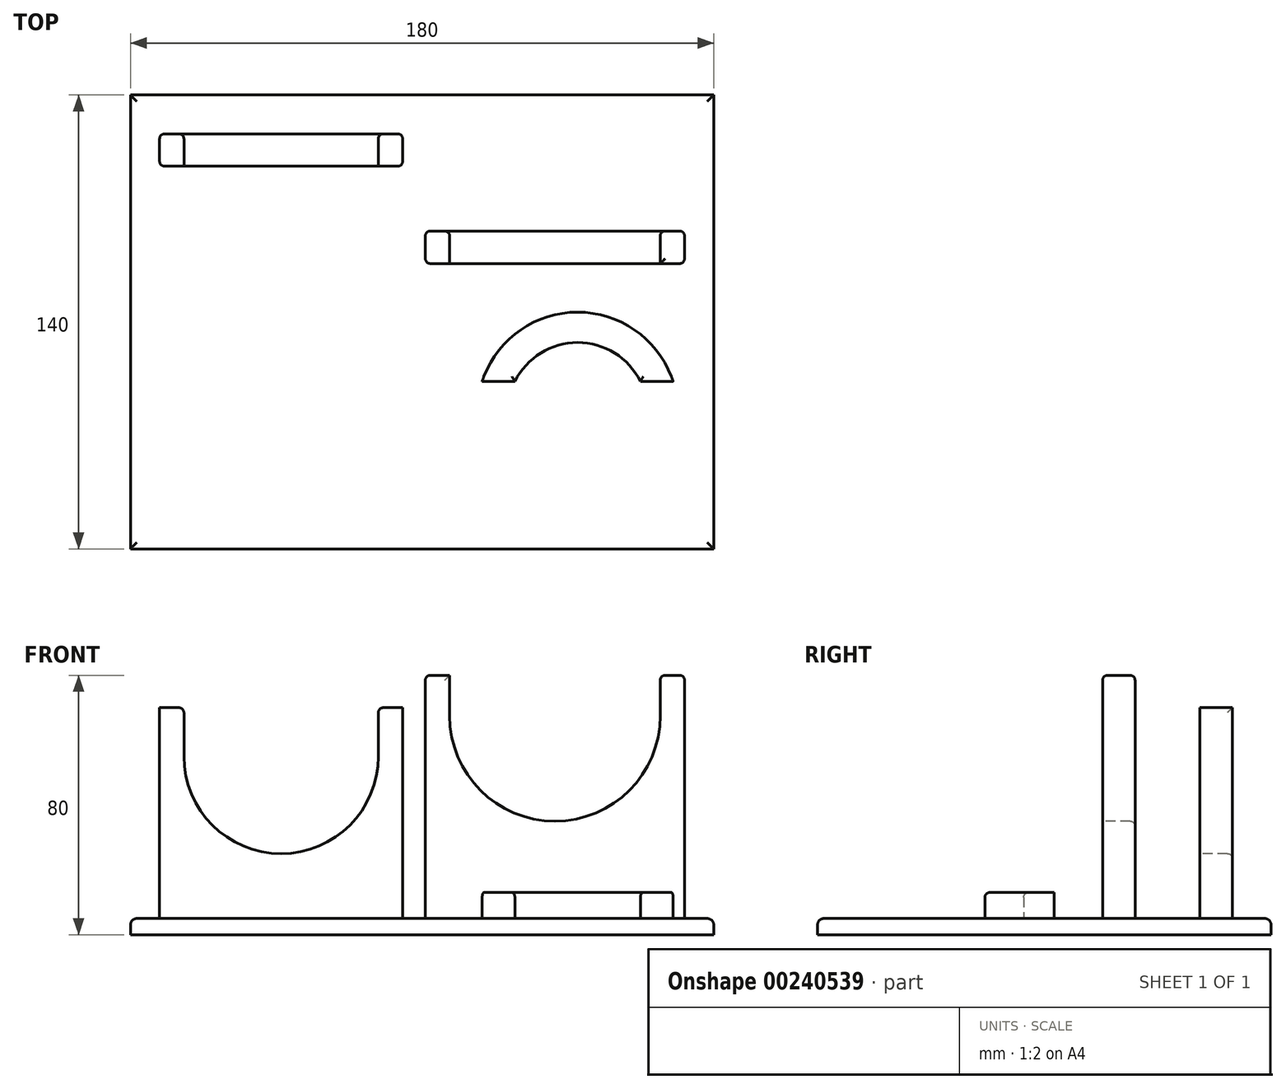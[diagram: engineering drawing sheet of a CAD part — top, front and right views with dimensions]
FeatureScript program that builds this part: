
annotation { "Feature Type Name" : "Feature", "Feature Type Description" : "" }
export const myFeature = defineFeature(function(context is Context, id is Id, definition is map)
    precondition{}
    {
        {
            var Q0;
            Q0=qCreatedBy(makeId("Top.planeOp"),FACE);
            var sketch = newSketch(context, id + "F5", { "sketchPlane" : qUnion([Q0])});
            skLineSegment(sketch, "E0.bottom", {"start": v(-84.6, 104.11) * mm, "end": v(95.4, 104.11) * mm});
            skLineSegment(sketch, "E0.top", {"start": v(-84.6, -35.89) * mm, "end": v(95.4, -35.89) * mm});
            skLineSegment(sketch, "E0.left", {"start": v(-84.6, 104.11) * mm, "end": v(-84.6, -35.89) * mm});
            skLineSegment(sketch, "E0.right", {"start": v(95.4, 104.11) * mm, "end": v(95.4, -35.89) * mm});
            skSolve(sketch);
        }
        {
            var Q0;
            Q0 = qSketchRegion(id + "F5", true);
            extrude(context, id + "F0", {"entities" : qUnion([Q0]), "depth" : 5 * mm});
        }
        {
            var Q0;
            Q0=makeQuery(id+"F0.opExtrude","CAP_EDGE",EDGE,{"disambiguationData":[OSD([sQuery(id+"F5.wireOp",EDGE,"E0.top")])],"isStart":false});
            var Q1;
            Q1=makeQuery(id+"F0.opExtrude","CAP_EDGE",EDGE,{"disambiguationData":[OSD([sQuery(id+"F5.wireOp",EDGE,"E0.right")])],"isStart":false});
            var Q2;
            Q2=makeQuery(id+"F0.opExtrude","CAP_EDGE",EDGE,{"disambiguationData":[OSD([sQuery(id+"F5.wireOp",EDGE,"E0.left")])],"isStart":false});
            var Q3;
            Q3=makeQuery(id+"F0.opExtrude","CAP_EDGE",EDGE,{"disambiguationData":[OSD([sQuery(id+"F5.wireOp",EDGE,"E0.bottom")])],"isStart":false});
            fillet(context, id + "F1", {"entities" : qUnion([Q0, Q1, Q2, Q3]), "radius" : 2 * mm, "tangentPropagation" : true, "allowEdgeOverflow" : false});
        }
        {
            var Q0;
            Q0=makeQuery(id+"F0.opExtrude","CAP_FACE",FACE,{"disambiguationData":[OSD([sQuery(id+"F5.wireOp",EDGE,"E0.bottom"),sQuery(id+"F5.wireOp",EDGE,"E0.top"),sQuery(id+"F5.wireOp",EDGE,"E0.left"),sQuery(id+"F5.wireOp",EDGE,"E0.right")])],"isStart":false});
            var sketch = newSketch(context, id + "F6", { "sketchPlane" : qUnion([Q0])});
            skLineSegment(sketch, "E1.bottom", {"start": v(23.95, 15.78) * mm, "end": v(34.04, 15.78) * mm});
            skLineSegment(sketch, "E2.trimOffspring", {"start": v(72.77, 15.78) * mm, "end": v(82.86, 15.78) * mm});
            skArc(sketch, "E3.trimOffspring", {"start": v(72.77, 15.78) * mm, "mid": v(53.4, 27.76) * mm, "end": v(34.04, 15.78) * mm});
            skArc(sketch, "E4.trimOffspring", {"start": v(82.86, 15.78) * mm, "mid": v(53.4, 37.11) * mm, "end": v(23.95, 15.78) * mm});
            skSolve(sketch);
        }
        {
            var Q0;
            Q0 = qSketchRegion(id + "F6", true);
            extrude(context, id + "F7", {"entities" : qUnion([Q0]), "operationType" : NewBodyOperationType.ADD, "depth" : 8 * mm});
        }
        {
            var Q0;
            Q0=makeQuery(id+"F0.opExtrude","CAP_FACE",FACE,{"disambiguationData":[OSD([sQuery(id+"F5.wireOp",EDGE,"E0.bottom"),sQuery(id+"F5.wireOp",EDGE,"E0.top"),sQuery(id+"F5.wireOp",EDGE,"E0.left"),sQuery(id+"F5.wireOp",EDGE,"E0.right")])],"isStart":false});
            var sketch = newSketch(context, id + "F8", { "sketchPlane" : qUnion([Q0])});
            skLineSegment(sketch, "E5.bottom", {"start": v(-75.6, 92.11) * mm, "end": v(-0.6, 92.11) * mm});
            skLineSegment(sketch, "E5.top", {"start": v(-75.6, 82.11) * mm, "end": v(-0.6, 82.11) * mm});
            skLineSegment(sketch, "E5.left", {"start": v(-75.6, 92.11) * mm, "end": v(-75.6, 82.11) * mm});
            skLineSegment(sketch, "E5.right", {"start": v(-0.6, 92.11) * mm, "end": v(-0.6, 82.11) * mm});
            skLineSegment(sketch, "E6.bottom", {"start": v(6.4, 62.11) * mm, "end": v(86.4, 62.11) * mm});
            skLineSegment(sketch, "E6.top", {"start": v(6.4, 52.11) * mm, "end": v(86.4, 52.11) * mm});
            skLineSegment(sketch, "E6.left", {"start": v(6.4, 62.11) * mm, "end": v(6.4, 52.11) * mm});
            skLineSegment(sketch, "E6.right", {"start": v(86.4, 62.11) * mm, "end": v(86.4, 52.11) * mm});
            skArc(sketch, "E7.0", {"start": v(82.86, 15.78) * mm, "mid": v(53.4, 37.11) * mm, "end": v(23.95, 15.78) * mm});
            skSolve(sketch);
        }
        {
            var Q0;
            Q0 = qSketchRegion(id + "F8", true);
            extrude(context, id + "F9", {"entities" : qUnion([Q0]), "operationType" : NewBodyOperationType.ADD, "depth" : 75 * mm});
        }
        {
            var Q0;
            Q0 = qSketchRegion(id + "F8", true);
            extrude(context, id + "F10", {"entities" : qUnion([Q0]), "operationType" : NewBodyOperationType.ADD, "depth" : 75 * mm});
        }
        {
            var Q0;
            Q0=makeQuery(id+"F9.opExtrude","SWEPT_FACE",FACE,{"disambiguationData":[OSD([sQuery(id+"F8.wireOp",EDGE,"E6.top")])]});
            var sketch = newSketch(context, id + "F2", { "sketchPlane" : qUnion([Q0])});
            skArc(sketch, "E8", {"start": v(13.9, 67.5) * mm, "mid": v(46.4, 35) * mm, "end": v(78.9, 67.5) * mm});
            skLineSegment(sketch, "E9.0", {"start": v(13.9, 80) * mm, "end": v(78.9, 80) * mm});
            skPoint(sketch, "E9.1", {"position": v(6.4, 80) * mm});
            skLineSegment(sketch, "E10", {"start": v(13.9, 80) * mm, "end": v(13.9, 67.5) * mm});
            skLineSegment(sketch, "E11", {"start": v(78.9, 67.5) * mm, "end": v(78.9, 80) * mm});
            skPoint(sketch, "E9.2.end.orphan", {"position": v(86.4, 5) * mm});
            skPoint(sketch, "E9.2.start.orphan", {"position": v(86.4, 80) * mm});
            skPoint(sketch, "E9.3.end.orphan", {"position": v(6.4, 5) * mm});
            skSolve(sketch);
        }
        {
            var Q0;
            Q0 = qSketchRegion(id + "F2", true);
            extrude(context, id + "F11", {"entities" : qUnion([Q0]), "operationType" : NewBodyOperationType.REMOVE, "oppositeDirection" : true, "depth" : 25 * mm});
        }
        {
            var Q0;
            Q0=makeQuery(id+"F9.opExtrude","SWEPT_FACE",FACE,{"disambiguationData":[OSD([sQuery(id+"F8.wireOp",EDGE,"E5.top")])]});
            var sketch = newSketch(context, id + "F3", { "sketchPlane" : qUnion([Q0])});
            skArc(sketch, "E12", {"start": v(-68.1, 55) * mm, "mid": v(-38.1, 25) * mm, "end": v(-8.1, 55) * mm});
            skLineSegment(sketch, "E13.0", {"start": v(-0.6, 80) * mm, "end": v(-0.6, 5) * mm});
            skLineSegment(sketch, "E13.1", {"start": v(-75.6, 80) * mm, "end": v(-0.6, 80) * mm});
            skLineSegment(sketch, "E13.2", {"start": v(-75.6, 80) * mm, "end": v(-75.6, 5) * mm});
            skLineSegment(sketch, "E14", {"start": v(-68.1, 55) * mm, "end": v(-68.1, 70) * mm});
            skLineSegment(sketch, "E15", {"start": v(-8.1, 55) * mm, "end": v(-8.1, 70) * mm});
            skLineSegment(sketch, "E16", {"start": v(-0.6, 70) * mm, "end": v(-8.1, 70) * mm});
            skLineSegment(sketch, "E17.trimOffspring", {"start": v(-75.6, 70) * mm, "end": v(-68.1, 70) * mm});
            skLineSegment(sketch, "E18.trimOffspring", {"start": v(-68.1, 70) * mm, "end": v(-75.6, 70) * mm});
            skLineSegment(sketch, "E19.trimOffspring", {"start": v(-8.1, 70) * mm, "end": v(-0.6, 70) * mm});
            skSolve(sketch);
        }
        {
            var Q0;
            Q0 = qSketchRegion(id + "F3", true);
            extrude(context, id + "F4", {"entities" : qUnion([Q0]), "operationType" : NewBodyOperationType.REMOVE, "oppositeDirection" : true, "depth" : 25 * mm});
        }
        {
            var Q0;
            Q0=makeQuery(id+"F9.opExtrude","SWEPT_EDGE",EDGE,{"disambiguationData":[OSD([sQuery(id+"F8.wireOp",EDGE,"E6.top"),sQuery(id+"F8.wireOp",EDGE,"E6.right")])]});
            var Q1;
            Q1=makeQuery(id+"F9.opExtrude","SWEPT_EDGE",EDGE,{"disambiguationData":[OSD([sQuery(id+"F8.wireOp",EDGE,"E6.bottom"),sQuery(id+"F8.wireOp",EDGE,"E6.right")])]});
            var Q2;
            Q2=makeQuery(id+"F11.boolean.opBoolean","COPY",EDGE,{"derivedFrom":makeQuery(id+"F11.opExtrude","SWEPT_EDGE",EDGE,{"disambiguationData":[OSD([sQuery(id+"F8.wireOp",EDGE,"E6.top"),sQuery(id+"F2.wireOp",EDGE,"E9.0"),sQuery(id+"F2.wireOp",EDGE,"E11")])]})});
            var Q3;
            Q3=makeQuery(id+"F11.boolean.opBoolean","COPY",EDGE,{"derivedFrom":makeQuery(id+"F11.opExtrude","SWEPT_EDGE",EDGE,{"disambiguationData":[OSD([sQuery(id+"F8.wireOp",EDGE,"E6.top"),sQuery(id+"F2.wireOp",EDGE,"E9.0"),sQuery(id+"F2.wireOp",EDGE,"E10")])]})});
            var Q4;
            Q4=makeQuery(id+"F4.boolean.opBoolean","COPY",EDGE,{"derivedFrom":makeQuery(id+"F4.opExtrude","SWEPT_EDGE",EDGE,{"disambiguationData":[OSD([sQuery(id+"F3.wireOp",EDGE,"E15"),sQuery(id+"F3.wireOp",EDGE,"E19.trimOffspring")])]})});
            var Q5;
            Q5=makeQuery(id+"F4.boolean.opBoolean","COPY",EDGE,{"derivedFrom":makeQuery(id+"F4.opExtrude","SWEPT_EDGE",EDGE,{"disambiguationData":[OSD([sQuery(id+"F3.wireOp",EDGE,"E14"),sQuery(id+"F3.wireOp",EDGE,"E18.trimOffspring")])]})});
            var Q6;
            Q6=makeQuery(id+"F9.opExtrude","SWEPT_EDGE",EDGE,{"disambiguationData":[OSD([sQuery(id+"F8.wireOp",EDGE,"E6.top"),sQuery(id+"F8.wireOp",EDGE,"E6.left")])]});
            var Q7;
            Q7=makeQuery(id+"F9.opExtrude","SWEPT_EDGE",EDGE,{"disambiguationData":[OSD([sQuery(id+"F8.wireOp",EDGE,"E6.bottom"),sQuery(id+"F8.wireOp",EDGE,"E6.left")])]});
            var Q8;
            Q8=makeQuery(id+"F9.opExtrude","SWEPT_EDGE",EDGE,{"disambiguationData":[OSD([sQuery(id+"F8.wireOp",EDGE,"E5.top"),sQuery(id+"F8.wireOp",EDGE,"E5.left")])]});
            var Q9;
            Q9=makeQuery(id+"F9.opExtrude","SWEPT_EDGE",EDGE,{"disambiguationData":[OSD([sQuery(id+"F8.wireOp",EDGE,"E5.bottom"),sQuery(id+"F8.wireOp",EDGE,"E5.left")])]});
            var Q10;
            Q10=makeQuery(id+"F9.opExtrude","SWEPT_EDGE",EDGE,{"disambiguationData":[OSD([sQuery(id+"F8.wireOp",EDGE,"E5.top"),sQuery(id+"F8.wireOp",EDGE,"E5.right")])]});
            var Q11;
            Q11=makeQuery(id+"F9.opExtrude","SWEPT_EDGE",EDGE,{"disambiguationData":[OSD([sQuery(id+"F8.wireOp",EDGE,"E5.bottom"),sQuery(id+"F8.wireOp",EDGE,"E5.right")])]});
            var Q12;
            Q12=makeQuery(id+"F9.opExtrude","CAP_EDGE",EDGE,{"disambiguationData":[OSD([sQuery(id+"F8.wireOp",EDGE,"E6.right")])],"isStart":false});
            var Q13;
            Q13=makeQuery(id+"F9.opExtrude","CAP_EDGE",EDGE,{"disambiguationData":[OSD([sQuery(id+"F8.wireOp",EDGE,"E6.left")])],"isStart":false});
            var Q14;
            Q14=makeQuery(id+"F4.boolean.opBoolean","COPY",EDGE,{"derivedFrom":makeQuery(id+"F4.opExtrude","SWEPT_EDGE",EDGE,{"disambiguationData":[OSD([sQuery(id+"F3.wireOp",EDGE,"E13.0"),sQuery(id+"F3.wireOp",EDGE,"E19.trimOffspring")])]})});
            var Q15;
            Q15=makeQuery(id+"F4.boolean.opBoolean","COPY",EDGE,{"derivedFrom":makeQuery(id+"F4.opExtrude","SWEPT_EDGE",EDGE,{"disambiguationData":[OSD([sQuery(id+"F3.wireOp",EDGE,"E13.2"),sQuery(id+"F3.wireOp",EDGE,"E18.trimOffspring")])]})});
            var Q16;
            {var subQ0=sQuery(id+"F8.wireOp",EDGE,"E6.left");var subQ1=sQuery(id+"F8.wireOp",EDGE,"E6.top");Q16=makeQuery(id+"F11.boolean.opBoolean","SPLIT",EDGE,{"disambiguationData":[TD([makeQuery(id+"F9.opExtrude","SWEPT_FACE",FACE,{"disambiguationData":[OSD([subQ0])]})])],"derivedFrom":makeQuery(id+"F9.opExtrude","CAP_EDGE",EDGE,{"disambiguationData":[OSD([subQ1])],"isStart":false})});}
            var Q17;
            Q17=makeQuery(id+"F4.boolean.opBoolean","COPY",EDGE,{"derivedFrom":makeQuery(id+"F4.opExtrude","CAP_EDGE",EDGE,{"disambiguationData":[OSD([sQuery(id+"F3.wireOp",EDGE,"E19.trimOffspring")])],"isStart":true})});
            var Q18;
            Q18=makeQuery(id+"F4.boolean.opBoolean","INTERSECT",EDGE,{"derivedFrom":[makeQuery(id+"F9.opExtrude","SWEPT_FACE",FACE,{"disambiguationData":[OSD([sQuery(id+"F8.wireOp",EDGE,"E5.bottom")])]}),makeQuery(id+"F4.opExtrude","SWEPT_FACE",FACE,{"disambiguationData":[OSD([sQuery(id+"F3.wireOp",EDGE,"E18.trimOffspring")])]})]});
            var Q19;
            Q19=makeQuery(id+"F4.boolean.opBoolean","INTERSECT",EDGE,{"derivedFrom":[makeQuery(id+"F9.opExtrude","SWEPT_FACE",FACE,{"disambiguationData":[OSD([sQuery(id+"F8.wireOp",EDGE,"E5.bottom")])]}),makeQuery(id+"F4.opExtrude","SWEPT_FACE",FACE,{"disambiguationData":[OSD([sQuery(id+"F3.wireOp",EDGE,"E19.trimOffspring")])]})]});
            var Q20;
            Q20=makeQuery(id+"F4.boolean.opBoolean","COPY",EDGE,{"derivedFrom":makeQuery(id+"F4.opExtrude","CAP_EDGE",EDGE,{"disambiguationData":[OSD([sQuery(id+"F3.wireOp",EDGE,"E18.trimOffspring")])],"isStart":true})});
            var Q21;
            {var subQ0=sQuery(id+"F8.wireOp",EDGE,"E6.bottom");var subQ1=sQuery(id+"F8.wireOp",EDGE,"E6.left");Q21=makeQuery(id+"F11.boolean.opBoolean","SPLIT",EDGE,{"disambiguationData":[TD([makeQuery(id+"F9.opExtrude","SWEPT_FACE",FACE,{"disambiguationData":[OSD([subQ1])]})])],"derivedFrom":makeQuery(id+"F9.opExtrude","CAP_EDGE",EDGE,{"disambiguationData":[OSD([subQ0])],"isStart":false})});}
            var Q22;
            {var subQ0=sQuery(id+"F8.wireOp",EDGE,"E6.right");var subQ1=sQuery(id+"F8.wireOp",EDGE,"E6.top");Q22=makeQuery(id+"F11.boolean.opBoolean","SPLIT",EDGE,{"disambiguationData":[TD([makeQuery(id+"F9.opExtrude","SWEPT_FACE",FACE,{"disambiguationData":[OSD([subQ0])]})])],"derivedFrom":makeQuery(id+"F9.opExtrude","CAP_EDGE",EDGE,{"disambiguationData":[OSD([subQ1])],"isStart":false})});}
            var Q23;
            Q23=makeQuery(id+"F11.boolean.opBoolean","COPY",EDGE,{"derivedFrom":makeQuery(id+"F11.opExtrude","CAP_EDGE",EDGE,{"disambiguationData":[OSD([sQuery(id+"F2.wireOp",EDGE,"E8")])],"isStart":true})});
            var Q24;
            Q24=makeQuery(id+"F4.boolean.opBoolean","COPY",EDGE,{"derivedFrom":makeQuery(id+"F4.opExtrude","CAP_EDGE",EDGE,{"disambiguationData":[OSD([sQuery(id+"F3.wireOp",EDGE,"E12")])],"isStart":true})});
            var Q25;
            {var subQ0=sQuery(id+"F8.wireOp",EDGE,"E6.bottom");var subQ1=sQuery(id+"F8.wireOp",EDGE,"E6.right");Q25=makeQuery(id+"F11.boolean.opBoolean","SPLIT",EDGE,{"disambiguationData":[TD([makeQuery(id+"F9.opExtrude","SWEPT_FACE",FACE,{"disambiguationData":[OSD([subQ1])]})])],"derivedFrom":makeQuery(id+"F9.opExtrude","CAP_EDGE",EDGE,{"disambiguationData":[OSD([subQ0])],"isStart":false})});}
            var Q26;
            Q26=makeQuery(id+"F11.boolean.opBoolean","INTERSECT",EDGE,{"derivedFrom":[makeQuery(id+"F9.opExtrude","SWEPT_FACE",FACE,{"disambiguationData":[OSD([sQuery(id+"F8.wireOp",EDGE,"E6.bottom")])]}),makeQuery(id+"F11.opExtrude","SWEPT_FACE",FACE,{"disambiguationData":[OSD([sQuery(id+"F2.wireOp",EDGE,"E8")])]})]});
            var Q27;
            Q27=makeQuery(id+"F4.boolean.opBoolean","INTERSECT",EDGE,{"derivedFrom":[makeQuery(id+"F9.opExtrude","SWEPT_FACE",FACE,{"disambiguationData":[OSD([sQuery(id+"F8.wireOp",EDGE,"E5.bottom")])]}),makeQuery(id+"F4.opExtrude","SWEPT_FACE",FACE,{"disambiguationData":[OSD([sQuery(id+"F3.wireOp",EDGE,"E12")])]})]});
            var Q28;
            Q28=makeQuery(id+"F7.opExtrude","CAP_EDGE",EDGE,{"disambiguationData":[OSD([sQuery(id+"F6.wireOp",EDGE,"E3.trimOffspring")])],"isStart":false});
            var Q29;
            Q29=makeQuery(id+"F7.opExtrude","CAP_EDGE",EDGE,{"disambiguationData":[OSD([sQuery(id+"F6.wireOp",EDGE,"E1.bottom")])],"isStart":false});
            var Q30;
            Q30=makeQuery(id+"F7.opExtrude","CAP_EDGE",EDGE,{"disambiguationData":[OSD([sQuery(id+"F6.wireOp",EDGE,"E2.trimOffspring")])],"isStart":false});
            fillet(context, id + "F12", {"entities" : qUnion([Q0, Q1, Q2, Q3, Q4, Q5, Q6, Q7, Q8, Q9, Q10, Q11, Q12, Q13, Q14, Q15, Q16, Q17, Q18, Q19, Q20, Q21, Q22, Q23, Q24, Q25, Q26, Q27, Q28, Q29, Q30]), "radius" : 1.5 * mm, "tangentPropagation" : true, "allowEdgeOverflow" : false});
        }
    });
